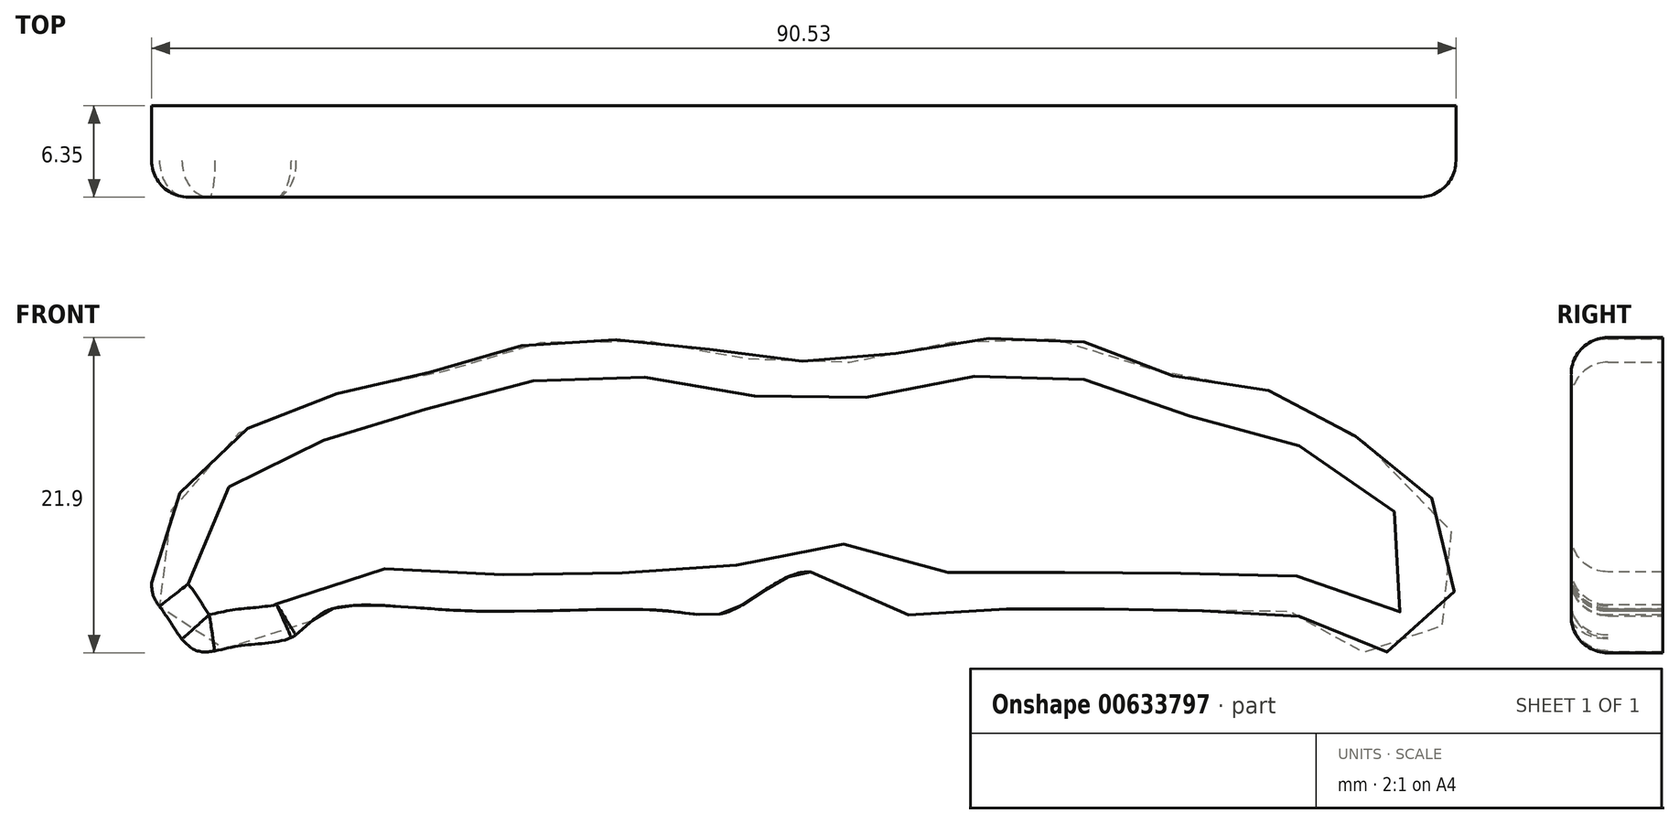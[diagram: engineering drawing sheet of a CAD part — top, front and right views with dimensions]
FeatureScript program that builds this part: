
annotation { "Feature Type Name" : "Feature", "Feature Type Description" : "" }
export const myFeature = defineFeature(function(context is Context, id is Id, definition is map)
    precondition{}
    {
        {
            var Q0;
            Q0=qCreatedBy(makeId("Front.planeOp"),FACE);
            var sketch = newSketch(context, id + "F0", { "sketchPlane" : qUnion([Q0])});
            skFitSpline(sketch, "E0", {"points": [v(3.7, 1.3) * mm, v(-1.82, -1.4) * mm, v(-6.32, -1.4) * mm, v(-20.28, -1.4) * mm, v(-29.85, -1.4) * mm, v(-32.21, -3.2) * mm, v(-36.15, -3.88) * mm, v(-39.08, -4.1) * mm, v(-41.1, -1.63) * mm, v(-42, 0) * mm, v(-40.88, 5.01) * mm, v(-38.52, 8.95) * mm, v(-35.03, 11.43) * mm, v(-30.52, 13) * mm, v(-26.13, 14.92) * mm, v(-21.63, 15.26) * mm, v(-19.04, 16.27) * mm, v(-13.64, 17.4) * mm, v(-9.36, 17.4) * mm, v(-4.63, 17.06) * mm, v(-1.03, 16.16) * mm, v(3.13, 15.93) * mm, v(7.19, 15.93) * mm, v(11.12, 16.83) * mm, v(16.2, 17.5) * mm, v(20.13, 17.5) * mm, v(24.74, 16.72) * mm, v(28.35, 15.03) * mm, v(34.54, 14.13) * mm, v(38.14, 12.67) * mm, v(42.64, 9.97) * mm, v(47.6, 5.35) * mm, v(48.5, 1.52) * mm, v(47.7, -2.2) * mm, v(45.46, -3.88) * mm, v(42.53, -4.33) * mm, v(39.72, -3.54) * mm, v(37.35, -1.63) * mm, v(33.98, -1.4) * mm, v(26.32, -1.29) * mm, v(17.32, -1.29) * mm, v(12.14, -1.4) * mm, v(8.42, -1.51) * mm, v(3.7, 1.3) * mm]});
            skSolve(sketch);
        }
        {
            var Q0;
            Q0 = qSketchRegion(id + "F0", true);
            extrude(context, id + "F1", {"entities" : qUnion([Q0]), "depth" : 6.35 * mm, "offsetDistance" : 25.4 * mm});
        }
        {
            var Q0;
            Q0=makeQuery(id+"F1.opExtrude","CAP_EDGE",EDGE,{"disambiguationData":[OSD([sQuery(id+"F0.wireOp",EDGE,"E0")])],"isStart":false});
            fillet(context, id + "F2", {"entities" : qUnion([Q0]), "radius" : 2.54 * mm, "tangentPropagation" : true, "allowEdgeOverflow" : false});
        }
    });
